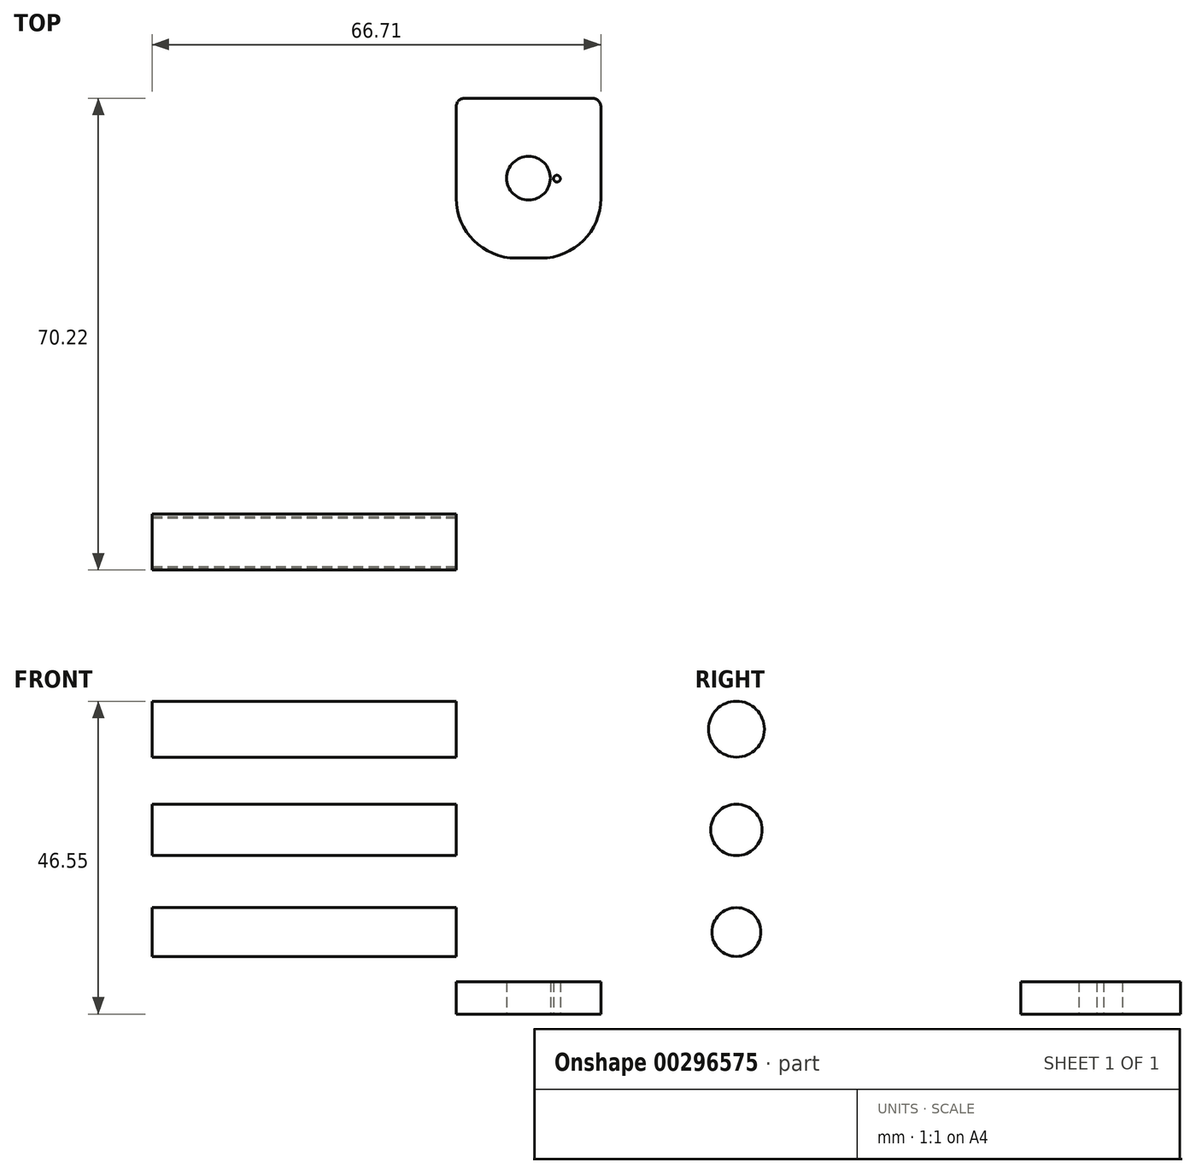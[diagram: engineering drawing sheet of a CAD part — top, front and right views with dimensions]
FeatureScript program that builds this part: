
annotation { "Feature Type Name" : "Feature", "Feature Type Description" : "" }
export const myFeature = defineFeature(function(context is Context, id is Id, definition is map)
    precondition{}
    {
        {
            var Q0;
            Q0=qCreatedBy(makeId("Top.planeOp"),FACE);
            var sketch = newSketch(context, id + "F0", { "sketchPlane" : qUnion([Q0])});
            skLineSegment(sketch, "E0.bottom", {"start": v(0, 0) * mm, "end": v(21.5, 0) * mm});
            skLineSegment(sketch, "E0.top", {"start": v(0, 23.8) * mm, "end": v(21.5, 23.8) * mm});
            skLineSegment(sketch, "E0.left", {"start": v(0, 0) * mm, "end": v(0, 23.8) * mm});
            skLineSegment(sketch, "E0.right", {"start": v(21.5, 0) * mm, "end": v(21.5, 23.8) * mm});
            skPoint(sketch, "E1.centerSnap0", {"position": v(0, 11.9) * mm});
            skPoint(sketch, "E1.centerSnap1", {"position": v(10.75, 23.8) * mm});
            skPoint(sketch, "E2.centerSnap0", {"position": v(10.75, 0) * mm});
            skCircle(sketch, "E3", {"center": v(10.75, 11.9) * mm, "radius": 3.25 * mm});
            skCircle(sketch, "E4", {"center": v(14.97, 11.83) * mm, "radius": 0.5 * mm});
            skSolve(sketch);
        }
        {
            var Q0;
            Q0 = qSketchRegion(id + "F0", true);
            extrude(context, id + "F1", {"entities" : qUnion([Q0]), "depth" : 4.8 * mm});
        }
        {
            var Q0;
            Q0=makeQuery(id+"F1.opExtrude","SWEPT_EDGE",EDGE,{"disambiguationData":[OSD([sQuery(id+"F0.wireOp",EDGE,"E0.bottom"),sQuery(id+"F0.wireOp",EDGE,"E0.right")])]});
            var Q1;
            Q1=makeQuery(id+"F1.opExtrude","SWEPT_EDGE",EDGE,{"disambiguationData":[OSD([sQuery(id+"F0.wireOp",EDGE,"E0.bottom"),sQuery(id+"F0.wireOp",EDGE,"E0.left")])]});
            fillet(context, id + "F2", {"entities" : qUnion([Q0, Q1]), "radius" : 8.9 * mm, "tangentPropagation" : true, "allowEdgeOverflow" : false});
        }
        {
            var Q0;
            Q0=makeQuery(id+"F1.opExtrude","SWEPT_EDGE",EDGE,{"disambiguationData":[OSD([sQuery(id+"F0.wireOp",EDGE,"E0.top"),sQuery(id+"F0.wireOp",EDGE,"E0.right")])]});
            var Q1;
            Q1=makeQuery(id+"F1.opExtrude","SWEPT_EDGE",EDGE,{"disambiguationData":[OSD([sQuery(id+"F0.wireOp",EDGE,"E0.top"),sQuery(id+"F0.wireOp",EDGE,"E0.left")])]});
            fillet(context, id + "F3", {"entities" : qUnion([Q0, Q1]), "radius" : 1.27 * mm, "tangentPropagation" : true, "allowEdgeOverflow" : false});
        }
        {
            var Q0;
            Q0=qCreatedBy(makeId("Front.planeOp"),FACE);
            var sketch = newSketch(context, id + "F4", { "sketchPlane" : qUnion([Q0])});
            skCircle(sketch, "E5", {"center": v(-5.9, 5.55) * mm, "radius": 4.9 * mm});
            skSolve(sketch);
        }
        {
            var Q0;
            Q0 = qSketchRegion(id + "F4", true);
            extrude(context, id + "F5", {"entities" : qUnion([Q0]), "operationType" : NewBodyOperationType.REMOVE, "oppositeDirection" : true, "depth" : 20.83 * mm});
        }
        {
            var Q0;
            Q0=qCreatedBy(makeId("Front.planeOp"),FACE);
            var sketch = newSketch(context, id + "F6", { "sketchPlane" : qUnion([Q0])});
            skCircle(sketch, "E6", {"center": v(-5.94, 5.5) * mm, "radius": 3.35 * mm});
            skSolve(sketch);
        }
        {
            var Q0;
            Q0 = qSketchRegion(id + "F6", true);
            extrude(context, id + "F7", {"entities" : qUnion([Q0]), "operationType" : NewBodyOperationType.REMOVE, "oppositeDirection" : true, "depth" : 25.4 * mm});
        }
        {
            var Q0;
            Q0=qCreatedBy(makeId("Right.planeOp"),FACE);
            var sketch = newSketch(context, id + "F8", { "sketchPlane" : qUnion([Q0])});
            skCircle(sketch, "E7", {"center": v(-42.26, 12.2) * mm, "radius": 3.63 * mm});
            skCircle(sketch, "E8", {"center": v(-42.26, 27.4) * mm, "radius": 3.82 * mm});
            skCircle(sketch, "E9", {"center": v(-42.26, 42.39) * mm, "radius": 4.16 * mm});
            skSolve(sketch);
        }
        {
            var Q0;
            Q0 = qSketchRegion(id + "F8", true);
            extrude(context, id + "F9", {"entities" : qUnion([Q0]), "operationType" : NewBodyOperationType.ADD, "oppositeDirection" : true, "depth" : 45.2 * mm});
        }
    });
